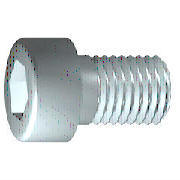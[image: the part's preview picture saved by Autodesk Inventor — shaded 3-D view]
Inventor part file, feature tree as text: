
AUTODESK INVENTOR PART (.ipt)
format: ipt  version: 2017 (Build 210142000, 142)  size: 184,832 bytes
history: native  units: mm (DEFAULTED — no unit token found)
features: sketch x2, extrude x1, plane x1, fillet x1
ambient origin geometry x7: Origin, YZ Plane, XY Plane, X Axis, Y Axis, Z Axis, Center Point
bodies: Solid1 (feature_tree), Body (feature_tree)
feature tree (5):
  extrude  "Slot"  Depth=5.0mm
  plane  "Work Plane1"
  fillet  "Fillet2"  Radius=5.0mm
  sketch  "Sketch1"  dims[d1=22.0mm d2=0.49086mm d3=5.0mm]
  sketch  "Sketch2"  dims[d4=2.5mm d5=60.0deg d6=5.0mm d7=5.0mm d8=4.618802mm d9=8.5mm d10=90.0deg d11=10.0mm d12=0.0mm d13=22.0mm d14=0.0mm d15=0.49076mm d16=0.49076mm d17=0.5mm d19=0.0mm d26=35.0mm d27=45.0deg d28=0.0mm d29=0.0mm d30=0.1mm]
